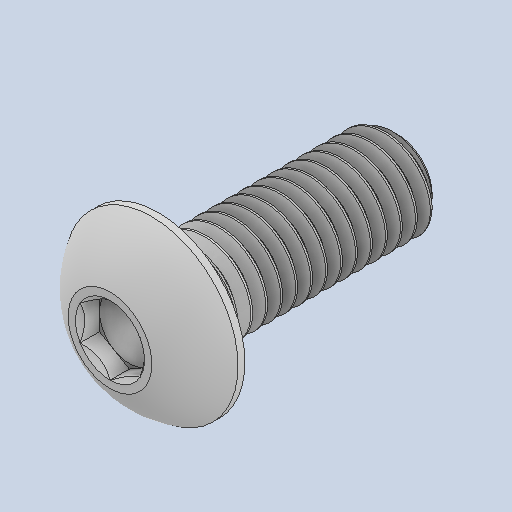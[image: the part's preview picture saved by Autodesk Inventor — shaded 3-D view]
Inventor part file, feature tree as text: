
AUTODESK INVENTOR PART (.ipt)
format: ipt  version: 2022.3 (Build 263350000, 350)  size: 576,000 bytes
history: native  units: in
note: dims shown in document units (in); Inventor stores cm internally (conversion verified against a paired STEP export)
features: revolve x1
ambient origin geometry x8: Origin, YZ Plane, XZ Plane, XY Plane, X Axis, Y Axis, Z Axis, Center Point
bodies: Solid1 (feature_tree)
feature tree (1):
  revolve  "Revolve2"  [1 undecoded]
note: 1 required parameter value undecoded (feature->parameter linkage not recoverable at this tier; creation-order binding heuristic only, values carry confidence <= 0.55)
